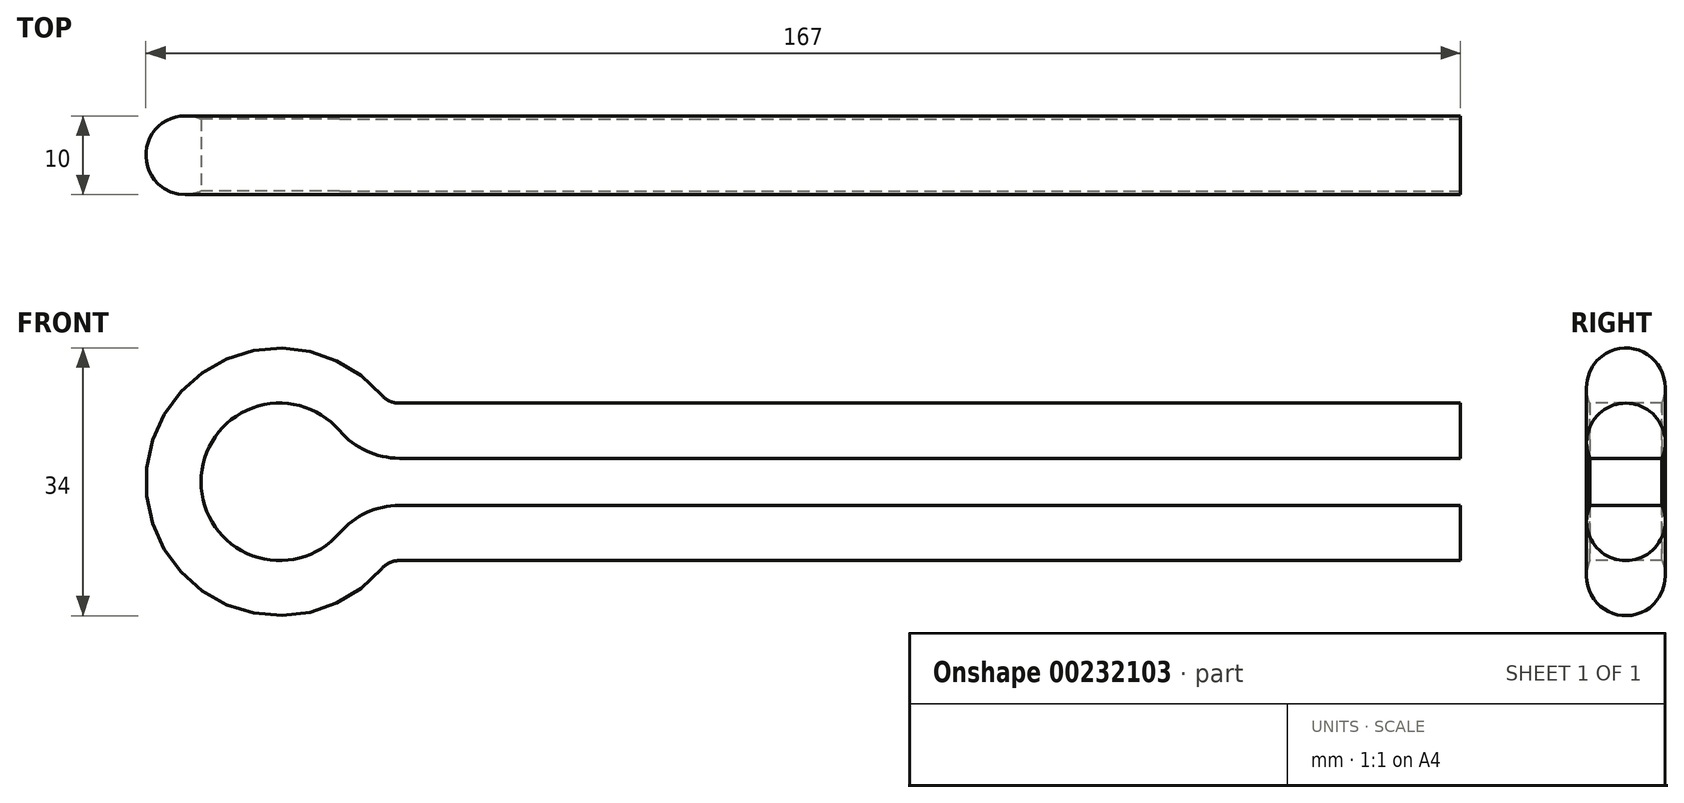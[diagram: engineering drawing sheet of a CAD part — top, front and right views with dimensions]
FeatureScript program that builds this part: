
annotation { "Feature Type Name" : "Feature", "Feature Type Description" : "" }
export const myFeature = defineFeature(function(context is Context, id is Id, definition is map)
    precondition{}
    {
        {
            var Q0;
            Q0=qCreatedBy(makeId("Front.planeOp"),FACE);
            var sketch = newSketch(context, id + "F0", { "sketchPlane" : qUnion([Q0])});
            skArc(sketch, "E0", {"start": v(7.6, 6.5) * mm, "mid": v(-10, 0) * mm, "end": v(7.6, -6.5) * mm});
            skLineSegment(sketch, "E1", {"start": v(15.2, 3) * mm, "end": v(150, 3) * mm});
            skLineSegment(sketch, "E2", {"start": v(0, 0) * mm, "end": v(150, 0) * mm, "construction": true});
            skLineSegment(sketch, "E3.MirrorCS", {"start": v(15.2, -3) * mm, "end": v(150, -3) * mm});
            skPoint(sketch, "E4.orphan", {"position": v(1.16, 3) * mm});
            skPoint(sketch, "E5.orphan", {"position": v(1.16, -3) * mm});
            skPoint(sketch, "E6.visualSharp", {"position": v(9.54, 3) * mm});
            skArc(sketch, "E6.filletArc", {"start": v(7.6, 6.5) * mm, "mid": v(11.02, 3.92) * mm, "end": v(15.2, 3) * mm});
            skPoint(sketch, "E7.visualSharp", {"position": v(9.54, -3) * mm});
            skArc(sketch, "E7.filletArc", {"start": v(15.2, -3) * mm, "mid": v(11.02, -3.92) * mm, "end": v(7.6, -6.5) * mm});
            skSolve(sketch);
        }
        {
            var Q0;
            Q0=qCreatedBy(makeId("Right.planeOp"),FACE);
            var Q1;
            Q1=sQuery(id+"F0.wireOp",VERTEX,"E1.end");
            cPlane(context, id + "F1", {"entities" : qUnion([Q0, Q1]), "cplaneType" : CPlaneType.PLANE_POINT, "offset" : 25 * mm, "width" : 150 * mm, "height" : 150 * mm});
        }
        {
            var Q0;
            Q0=qCreatedBy(id+"F1.planeOp",FACE);
            var sketch = newSketch(context, id + "F2", { "sketchPlane" : qUnion([Q0])});
            skArc(sketch, "E8", {"start": v(4.58, 3) * mm, "mid": v(0, 10) * mm, "end": v(-4.58, 3) * mm});
            skLineSegment(sketch, "E9", {"start": v(-4.58, 3) * mm, "end": v(4.58, 3) * mm});
            skLineSegment(sketch, "E10", {"start": v(0, 10) * mm, "end": v(0, 3) * mm, "construction": true});
            skSolve(sketch);
        }
        {
            var Q0;
            Q0=makeQuery(id+"F2.imprint","IMPRINT",FACE,{"disambiguationData":[TD([[makeQuery(id+"F2.imprint","IMPRINT",EDGE,{"derivedFrom":sQuery(id+"F2.wireOp",EDGE,"E8")}),1.0]])]});
            var Q1;
            Q1=sQuery(id+"F0.wireOp",EDGE,"E1");
            var Q2;
            Q2=sQuery(id+"F0.wireOp",EDGE,"E6.filletArc");
            var Q3;
            Q3=sQuery(id+"F0.wireOp",EDGE,"E0");
            var Q4;
            Q4=sQuery(id+"F0.wireOp",EDGE,"E7.filletArc");
            var Q5;
            Q5=sQuery(id+"F0.wireOp",EDGE,"E3.MirrorCS");
            sweep(context, id + "F3", {"profiles" : qUnion([Q0]), "path" : qUnion([Q1, Q2, Q3, Q4, Q5])});
        }
    });
